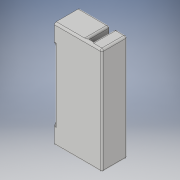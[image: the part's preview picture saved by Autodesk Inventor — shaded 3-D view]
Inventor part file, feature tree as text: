
AUTODESK INVENTOR PART (.ipt)
format: ipt  version: 2018 (Build 220112000, 112)  size: 437,760 bytes
history: native  units: in
note: dims shown in document units (in); Inventor stores cm internally (conversion verified against a paired STEP export)
features: reference x18, extrude x11, sketch x11, fillet x8, other x7, projected_geometry x4, plane x3
ambient origin geometry x8: Origin, YZ Plane, XZ Plane, XY Plane, X Axis, Y Axis, Z Axis, Center Point
bodies: Solid1 (feature_tree)
feature tree (62):
  extrude  "Extrusion1"  Depth=0.125in
  extrude  "Extrusion2"  Depth=0.4724in TaperAngle=0.0deg
  extrude  "Extrusion3"  Depth=0.2in TaperAngle=0.0deg
  extrude  "Extrusion4"  Depth=0.4in
  extrude  "Extrusion5"  Depth=0.25in
  extrude  "Extrusion6"  Depth=0.0787in TaperAngle=0.0deg
  fillet  "Fillet1"  Radius=0.125in
  fillet  "Fillet4"  Radius=0.1181in
  sketch  "Sketch8"  dims[d19=0.125in d20=0.1181in]
  plane  "Work Plane1"
  extrude  "Extrusion7"  Depth=0.1181in
  sketch  "Sketch9"  dims[d21=1.15in d22=0.0787in d23=0.0in d24=0.0394in d27=0.0394in d28=0.0197in d29=0.0197in]
  plane  "Work Plane2"
  extrude  "Extrusion8"  Depth=0.0394in TaperAngle=0.0deg
  fillet  "Fillet5"  Radius=0.0394in
  fillet  "Fillet6"  Radius=0.0394in
  fillet  "Fillet7"  Radius=0.0197in
  fillet  "Fillet9"  Radius=0.0197in
  sketch  "Sketch10"  dims[d30=1.0in d31=0.0in d32=0.0394in d33=0.0394in d34=1.0in d35=0.0in]
  plane  "Work Plane3"
  extrude  "Extrusion9"  Depth=0.0394in
  fillet  "Fillet10"  Radius=0.0394in
  fillet  "Fillet11"  Radius=1.0in
  extrude  "Extrusion10"  Depth=0.0394in
  extrude  "Extrusion11"  Depth=0.0394in
  sketch  "Sketch1"  dims[d0=0.5in d1=0.125in]
  reference  "Reference1"
  reference  "Reference2"
  reference  "Reference3"
  reference  "Reference4"
  reference  "Reference5"
  reference  "Reference6"
  reference  "Reference7"
  reference  "Reference8"
  reference  "Reference9"
  reference  "Reference10"
  reference  "Reference11"
  reference  "Reference12"
  reference  "Reference13"
  reference  "Reference14"
  reference  "Reference15"
  reference  "Reference16"
  reference  "Reference17"
  sketch  "Sketch2"  dims[d2=0.7in d3=0.4724in d4=0.0in]
  projected_geometry  "Projected Loop1"
  projected_geometry  "Projected Loop2"
  sketch  "Sketch4"  dims[d5=0.0787in d6=0.0in d7=0.2in d8=0.0in]
  projected_geometry  "Projected Loop3"
  sketch  "Sketch5"  dims[d9=0.4in d10=0.4in]
  reference  "Reference20"
  sketch  "Sketch6"  dims[d11=0.5512in d12=0.0in d13=0.25in]
  sketch  "Sketch7"  dims[d14=0.25in d15=0.0787in d16=0.0in d17=0.125in d18=0.1181in]
  projected_geometry  "Projected Loop4"
  sketch  "Sketch11"  dims[d36=0.0394in d37=0.0394in]
  sketch  "Sketch12"  dims[d38=0.0394in d40=0.0394in d41=0.0098in d42=1.0in d43=0.0in d44=0.0394in d45=0.0394in d46=12.0in d47=0.0in d48=0.128in d49=0.128in d50=0.315in d51=0.0in]
  other  "<userpath>\OneDrive\Documents\Inventor\TSA\2018\Animatronics\Tortoise\TurtleAssembly.iam"
  other  "TurtleAssembly.iam"
  other  "servo (2):1"
  other  "smallergear:4"
  other  "<userpath>\OneDrive\Documents\Inventor\TSA\2018\Animatronics\Tortoise\AssemblyTURTLE.iam"
  other  "AssemblyTURTLE.iam"
  other  "Frame:1"
